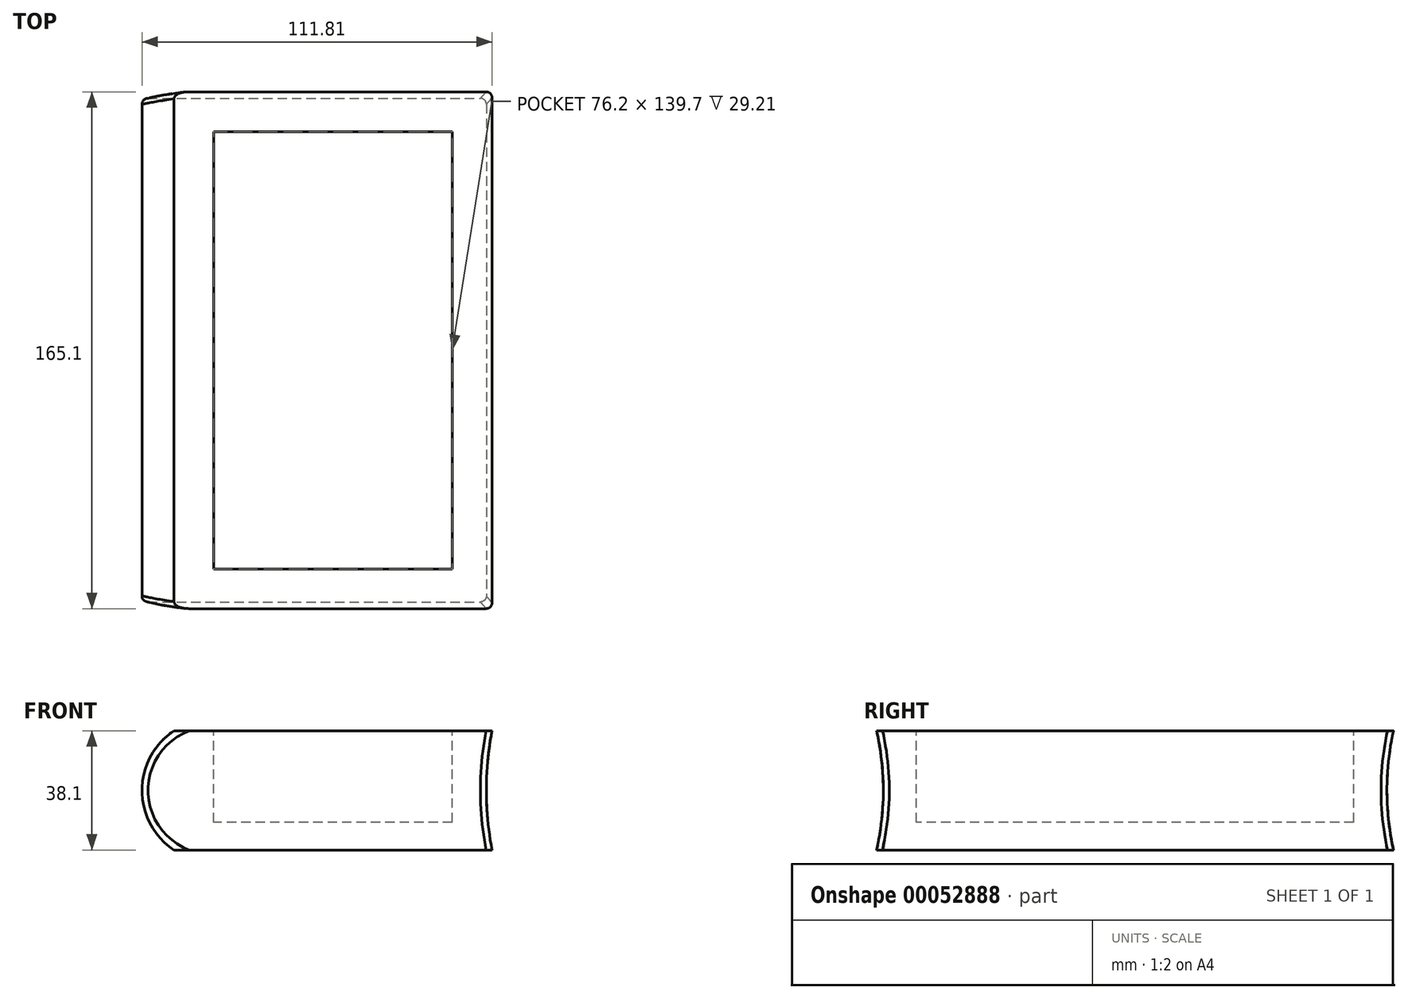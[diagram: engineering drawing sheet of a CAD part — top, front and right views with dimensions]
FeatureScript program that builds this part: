
annotation { "Feature Type Name" : "Feature", "Feature Type Description" : "" }
export const myFeature = defineFeature(function(context is Context, id is Id, definition is map)
    precondition{}
    {
        {
            var Q0;
            Q0=qCreatedBy(makeId("Top.planeOp"),FACE);
            var sketch = newSketch(context, id + "F0", { "sketchPlane" : qUnion([Q0])});
            skLineSegment(sketch, "E0.bottom", {"start": v(-47.58, 108.21) * mm, "end": v(54.02, 108.21) * mm});
            skLineSegment(sketch, "E0.top", {"start": v(-47.58, -56.89) * mm, "end": v(54.02, -56.89) * mm});
            skLineSegment(sketch, "E0.left", {"start": v(-47.58, 108.21) * mm, "end": v(-47.58, -56.89) * mm});
            skLineSegment(sketch, "E0.right", {"start": v(54.02, 108.21) * mm, "end": v(54.02, -56.89) * mm});
            skSolve(sketch);
        }
        {
            var Q0;
            Q0 = qSketchRegion(id + "F0", true);
            var Q1;
            Q1=makeQuery(id+"F0.imprint","IMPRINT",FACE,{"disambiguationData":[TD([[makeQuery(id+"F0.imprint","IMPRINT",EDGE,{"derivedFrom":sQuery(id+"F0.wireOp",EDGE,"E0.bottom")}),-1.0]])]});
            extrude(context, id + "F1", {"entities" : qUnion([Q0, Q1]), "depth" : 38.1 * mm});
        }
        {
            var Q0;
            Q0=makeQuery(id+"F1.opExtrude","CAP_FACE",FACE,{"disambiguationData":[OSD([sQuery(id+"F0.wireOp",EDGE,"E0.bottom"),sQuery(id+"F0.wireOp",EDGE,"E0.top"),sQuery(id+"F0.wireOp",EDGE,"E0.left"),sQuery(id+"F0.wireOp",EDGE,"E0.right")])],"isStart":false});
            var sketch = newSketch(context, id + "F2", { "sketchPlane" : qUnion([Q0])});
            skLineSegment(sketch, "E1.rect.bottom", {"start": v(41.32, 95.51) * mm, "end": v(-34.88, 95.51) * mm});
            skLineSegment(sketch, "E1.rect.top", {"start": v(41.32, -44.19) * mm, "end": v(-34.88, -44.19) * mm});
            skLineSegment(sketch, "E1.rect.left", {"start": v(41.32, 95.51) * mm, "end": v(41.32, -44.19) * mm});
            skLineSegment(sketch, "E1.rect.right", {"start": v(-34.88, 95.51) * mm, "end": v(-34.88, -44.19) * mm});
            skPoint(sketch, "E1.rect.middle", {"position": v(3.22, 25.66) * mm});
            skLineSegment(sketch, "E2.rect.bottom", {"start": v(-188.8, 94.86) * mm, "end": v(-265, 94.86) * mm});
            skLineSegment(sketch, "E2.rect.right", {"start": v(-265, 94.86) * mm, "end": v(-265, -44.84) * mm});
            skLineSegment(sketch, "E2.rect.top", {"start": v(-188.8, -44.84) * mm, "end": v(-265, -44.84) * mm});
            skLineSegment(sketch, "E2.rect.left", {"start": v(-188.8, 94.86) * mm, "end": v(-188.8, -44.84) * mm});
            skSolve(sketch);
        }
        {
            var Q0;
            Q0=makeQuery(id+"F2.imprint","IMPRINT",FACE,{"disambiguationData":[TD([[makeQuery(id+"F2.imprint","IMPRINT",EDGE,{"derivedFrom":sQuery(id+"F2.wireOp",EDGE,"E1.rect.bottom")}),1.0]])]});
            extrude(context, id + "F3", {"entities" : qUnion([Q0]), "operationType" : NewBodyOperationType.REMOVE, "oppositeDirection" : true, "depth" : 29.2 * mm});
        }
        {
            var Q0;
            Q0=makeQuery(id+"F1.opExtrude","SWEPT_FACE",FACE,{"disambiguationData":[OSD([sQuery(id+"F0.wireOp",EDGE,"E0.bottom")])]});
            var sketch = newSketch(context, id + "F4", { "sketchPlane" : qUnion([Q0])});
            skArc(sketch, "E3", {"start": v(47.58, 0) * mm, "mid": v(57.79, 19.05) * mm, "end": v(47.58, 38.1) * mm});
            skSolve(sketch);
        }
        {
            var Q0;
            Q0=makeQuery(id+"F4.imprint","IMPRINT",FACE,{"disambiguationData":[TD([[makeQuery(id+"F4.imprint","IMPRINT",EDGE,{"derivedFrom":sQuery(id+"F4.wireOp",EDGE,"E3")}),1.0]])]});
            extrude(context, id + "F5", {"entities" : qUnion([Q0]), "operationType" : NewBodyOperationType.ADD, "oppositeDirection" : true, "depth" : 165.1 * mm});
        }
        {
            var Q0;
            Q0=makeQuery(id+"F5.boolean.opBoolean","MERGE",FACE,{"derivedFrom":[makeQuery(id+"F1.opExtrude","SWEPT_FACE",FACE,{"disambiguationData":[OSD([sQuery(id+"F0.wireOp",EDGE,"E0.top")])]}),makeQuery(id+"F5.opExtrude","CAP_FACE",FACE,{"disambiguationData":[OSD([sQuery(id+"F0.wireOp",EDGE,"E0.bottom"),sQuery(id+"F0.wireOp",EDGE,"E0.left"),sQuery(id+"F4.wireOp",EDGE,"E3")])],"isStart":false})]});
            var sketch = newSketch(context, id + "F6", { "sketchPlane" : qUnion([Q0])});
            skArc(sketch, "E4", {"start": v(54.02, 38.1) * mm, "mid": v(52.2, 19.05) * mm, "end": v(54.02, 0) * mm});
            skSolve(sketch);
        }
        {
            var Q0;
            Q0=makeQuery(id+"F1.opExtrude","SWEPT_FACE",FACE,{"disambiguationData":[OSD([sQuery(id+"F0.wireOp",EDGE,"E0.right")])]});
            var sketch = newSketch(context, id + "F7", { "sketchPlane" : qUnion([Q0])});
            skArc(sketch, "E5", {"start": v(-56.89, 0) * mm, "mid": v(-54.74, 19.05) * mm, "end": v(-56.89, 38.1) * mm});
            skArc(sketch, "E6", {"start": v(108.21, 38.1) * mm, "mid": v(106.13, 19.05) * mm, "end": v(108.21, 0) * mm});
            skSolve(sketch);
        }
        {
            var Q0;
            Q0=makeQuery(id+"F7.imprint","IMPRINT",FACE,{"disambiguationData":[TD([[makeQuery(id+"F7.imprint","IMPRINT",EDGE,{"derivedFrom":sQuery(id+"F7.wireOp",EDGE,"E6")}),1.0]])]});
            var Q1;
            Q1=makeQuery(id+"F7.imprint","IMPRINT",FACE,{"disambiguationData":[TD([[makeQuery(id+"F7.imprint","IMPRINT",EDGE,{"derivedFrom":sQuery(id+"F7.wireOp",EDGE,"E5")}),1.0]])]});
            extrude(context, id + "F8", {"entities" : qUnion([Q0, Q1]), "operationType" : NewBodyOperationType.REMOVE, "oppositeDirection" : true, "depth" : 177.8 * mm});
        }
        {
            var Q0;
            Q0=makeQuery(id+"F6.imprint","IMPRINT",FACE,{"disambiguationData":[TD([[makeQuery(id+"F6.imprint","IMPRINT",EDGE,{"derivedFrom":sQuery(id+"F6.wireOp",EDGE,"E4")}),1.0]])]});
            extrude(context, id + "F9", {"entities" : qUnion([Q0]), "operationType" : NewBodyOperationType.REMOVE, "oppositeDirection" : true, "depth" : 203.2 * mm});
        }
        {
            var Q0;
            Q0=makeQuery(id+"F9.boolean.opBoolean","INTERSECT",EDGE,{"derivedFrom":[makeQuery(id+"F8.boolean.opBoolean","COPY",FACE,{"derivedFrom":makeQuery(id+"F8.opExtrude","SWEPT_FACE",FACE,{"disambiguationData":[OSD([sQuery(id+"F7.wireOp",EDGE,"E5")])]})}),makeQuery(id+"F9.opExtrude","SWEPT_FACE",FACE,{"disambiguationData":[OSD([sQuery(id+"F6.wireOp",EDGE,"E4")])]})]});
            var Q1;
            Q1=makeQuery(id+"F9.boolean.opBoolean","INTERSECT",EDGE,{"derivedFrom":[makeQuery(id+"F8.boolean.opBoolean","COPY",FACE,{"derivedFrom":makeQuery(id+"F8.opExtrude","SWEPT_FACE",FACE,{"disambiguationData":[OSD([sQuery(id+"F7.wireOp",EDGE,"E6")])]})}),makeQuery(id+"F9.opExtrude","SWEPT_FACE",FACE,{"disambiguationData":[OSD([sQuery(id+"F6.wireOp",EDGE,"E4")])]})]});
            fillet(context, id + "F10", {"entities" : qUnion([Q0, Q1]), "radius" : 1.9 * mm, "tangentPropagation" : true, "allowEdgeOverflow" : false});
        }
        {
            var Q0;
            Q0=makeQuery(id+"F8.boolean.opBoolean","INTERSECT",EDGE,{"derivedFrom":[makeQuery(id+"F5.opExtrude","SWEPT_FACE",FACE,{"disambiguationData":[OSD([sQuery(id+"F4.wireOp",EDGE,"E3")])]}),makeQuery(id+"F8.opExtrude","SWEPT_FACE",FACE,{"disambiguationData":[OSD([sQuery(id+"F7.wireOp",EDGE,"E5")])]})]});
            var Q1;
            Q1=makeQuery(id+"F8.boolean.opBoolean","INTERSECT",EDGE,{"derivedFrom":[makeQuery(id+"F5.opExtrude","SWEPT_FACE",FACE,{"disambiguationData":[OSD([sQuery(id+"F4.wireOp",EDGE,"E3")])]}),makeQuery(id+"F8.opExtrude","SWEPT_FACE",FACE,{"disambiguationData":[OSD([sQuery(id+"F7.wireOp",EDGE,"E6")])]})]});
            fillet(context, id + "F11", {"entities" : qUnion([Q0, Q1]), "radius" : 1.9 * mm, "tangentPropagation" : true, "allowEdgeOverflow" : false});
        }
    });
